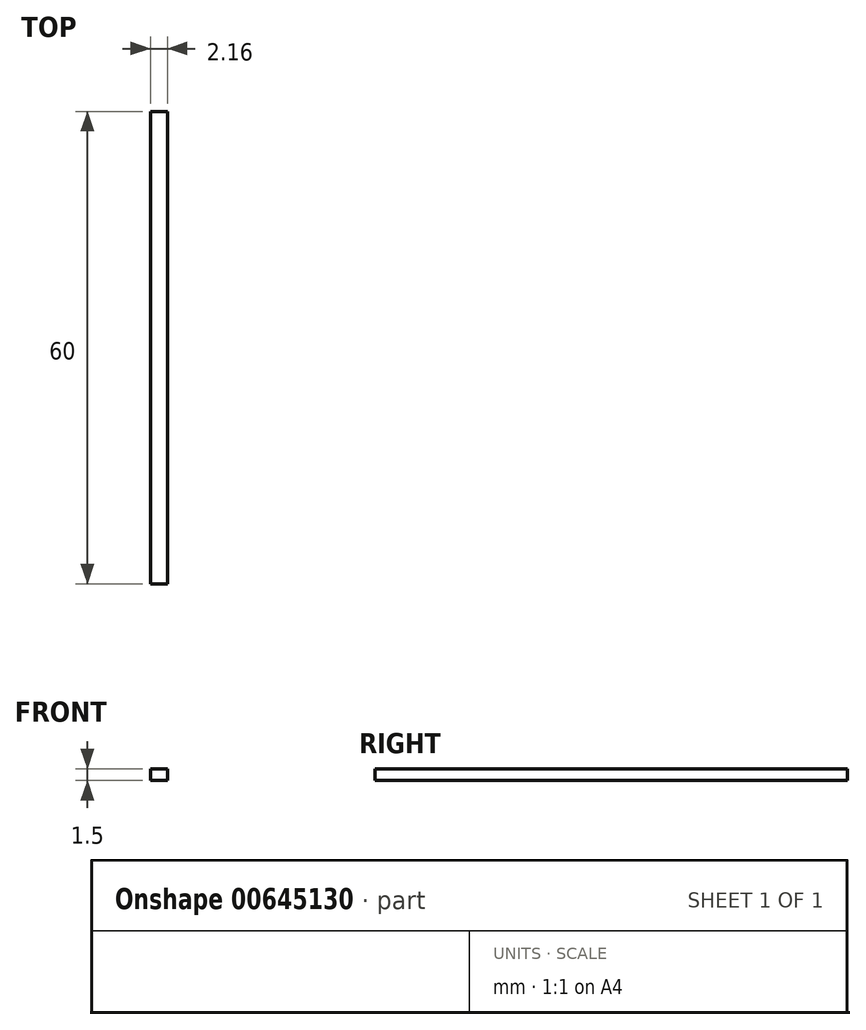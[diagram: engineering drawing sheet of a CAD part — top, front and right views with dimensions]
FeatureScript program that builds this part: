
annotation { "Feature Type Name" : "Feature", "Feature Type Description" : "" }
export const myFeature = defineFeature(function(context is Context, id is Id, definition is map)
    precondition{}
    {
        {
            var Q0;
            Q0=qCreatedBy(makeId("Top.planeOp"),FACE);
            var sketch = newSketch(context, id + "F0", { "sketchPlane" : qUnion([Q0])});
            skArc(sketch, "E0", {"start": v(-0.75, 1.39) * mm, "mid": v(1.5, -0.46) * mm, "end": v(-1.4, -0.74) * mm});
            skPoint(sketch, "E1", {"position": v(-1.08, 1.99) * mm});
            skPoint(sketch, "E2", {"position": v(-0.48, 0.88) * mm});
            skPoint(sketch, "E3", {"position": v(-0.88, -0.47) * mm});
            skArc(sketch, "E4", {"start": v(-1.08, 1.99) * mm, "mid": v(2.16, -0.65) * mm, "end": v(-2, -1.06) * mm});
            skLineSegment(sketch, "E5", {"start": v(-0.75, 1.39) * mm, "end": v(-1.08, 1.99) * mm});
            skLineSegment(sketch, "E6", {"start": v(-1.4, -0.74) * mm, "end": v(-2, -1.06) * mm});
            skLineSegment(sketch, "E7", {"start": v(-1.08, 1.99) * mm, "end": v(1.08, 1.99) * mm});
            skLineSegment(sketch, "E8", {"start": v(-1.08, 1.99) * mm, "end": v(-1.08, 61.99) * mm});
            skLineSegment(sketch, "E9", {"start": v(1.08, 1.99) * mm, "end": v(1.08, 61.99) * mm});
            skLineSegment(sketch, "E10", {"start": v(1.08, 61.99) * mm, "end": v(-1.08, 61.99) * mm});
            skSolve(sketch);
        }
        {
            var Q0;
            {var subQ0=sQuery(id+"F0.wireOp",EDGE,"E7");Q0=makeQuery(id+"F0.imprint","IMPRINT",FACE,{"disambiguationData":[TD([[makeQuery(id+"F0.imprint","IMPRINT",EDGE,{"derivedFrom":subQ0}),1.0]])]});}
            var Q1;
            {var subQ0=sQuery(id+"F0.wireOp",EDGE,"E8");Q1=makeQuery(id+"F0.imprint","IMPRINT",FACE,{"disambiguationData":[TD([[makeQuery(id+"F0.imprint","IMPRINT",EDGE,{"derivedFrom":subQ0}),-1.0]])]});}
            var Q2;
            Q2=makeQuery(id+"F0.imprint","IMPRINT",FACE,{"disambiguationData":[TD([[makeQuery(id+"F0.imprint","IMPRINT",EDGE,{"derivedFrom":sQuery(id+"F0.wireOp",EDGE,"E0")}),1.0]])]});
            extrude(context, id + "F1", {"entities" : qUnion([Q0, Q1, Q2]), "depth" : 1.5 * mm, "offsetDistance" : 25.4 * mm});
        }
    });
